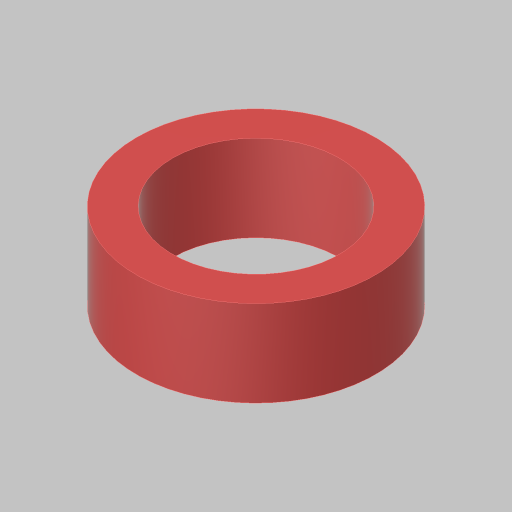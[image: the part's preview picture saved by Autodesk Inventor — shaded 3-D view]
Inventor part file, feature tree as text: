
AUTODESK INVENTOR PART (.ipt)
format: ipt  version: 2023.5 (Build 275446000, 446)  size: 97,792 bytes
history: native  units: in
note: dims shown in document units (in); Inventor stores cm internally (conversion verified against a paired STEP export)
features: extrude x1, sketch x1
ambient origin geometry x8: Origin, YZ Plane, XZ Plane, XY Plane, X Axis, Y Axis, Z Axis, Center Point
bodies: Solid1 (feature_tree)
feature tree (2):
  extrude  "Extrusion1"  Depth=0.3in
  sketch  "Sketch1"  dims[d0=0.58in d1=0.125in d2=0.3in d3=0.0in]
